# Revit family: 205_BSIL-100-_
name_source: partatom
category: Duct Accessories
units: mm (PartAtom-declared; Revit-internal decimal feet)

## family parameters
Always vertical = Yes
Cut with Voids When Loaded = No
Part Type = Breaks Into
Round Connector Dimension = Use Diameter
Shared = No
Work Plane-Based = No

## types (8) — shared parameters
CAT0 = Yes
Description = CIRCULAR CURVED
Manufacturer = Alnor
QmdConnectorList = 201;D;202;D
URL = http://www.ventilation-alnor.co.uk
magiPartTypeId = 205
magiProductFamilyId = BSIL-100-*

## per-type parameters (varying)
| type | CD | D | H2D | L | L2 | L2D | W2D |
| BSIL-100-125 | 315 mm  [stored 1.03346 ft] | 125 mm | 325 mm | 260 mm  [stored 0.853018 ft] | 252 mm | 260 mm  [stored 0.853018 ft] | 325 mm |
| BSIL-100-630 | 850 mm | 630 mm | 830 mm | 610 mm | 602 mm | 610 mm | 830 mm |
| BSIL-100-500 | 710 mm | 500 mm | 700 mm | 485 mm | 477 mm | 485 mm | 700 mm |
| BSIL-100-400 | 600 mm  [stored 1.9685 ft] | 400 mm | 600 mm  [stored 1.9685 ft] | 420 mm | 412 mm | 420 mm | 600 mm  [stored 1.9685 ft] |
| BSIL-100-315 | 500 mm | 315 mm | 515 mm | 375 mm | 367 mm | 375 mm | 515 mm |
| BSIL-100-250 | 450 mm | 250 mm | 450 mm | 370 mm | 362 mm | 370 mm | 450 mm |
| BSIL-100-200 | 400 mm | 200 mm | 400 mm | 325 mm | 317 mm | 325 mm | 400 mm |
| BSIL-100-160 | 355 mm | 160 mm | 360 mm | 280 mm | 272 mm | 280 mm | 360 mm |

note: column(s) folded — value = type name in every type: MC Product Code, magiProductId

note: [stored X ft] marks values corroborated as IEEE doubles in the binary element streams (Revit-internal decimal feet)

## geometry (parser evidence)
native form markers: Blend x2, Sweep x3
no freeform markers — native parametric forms only
